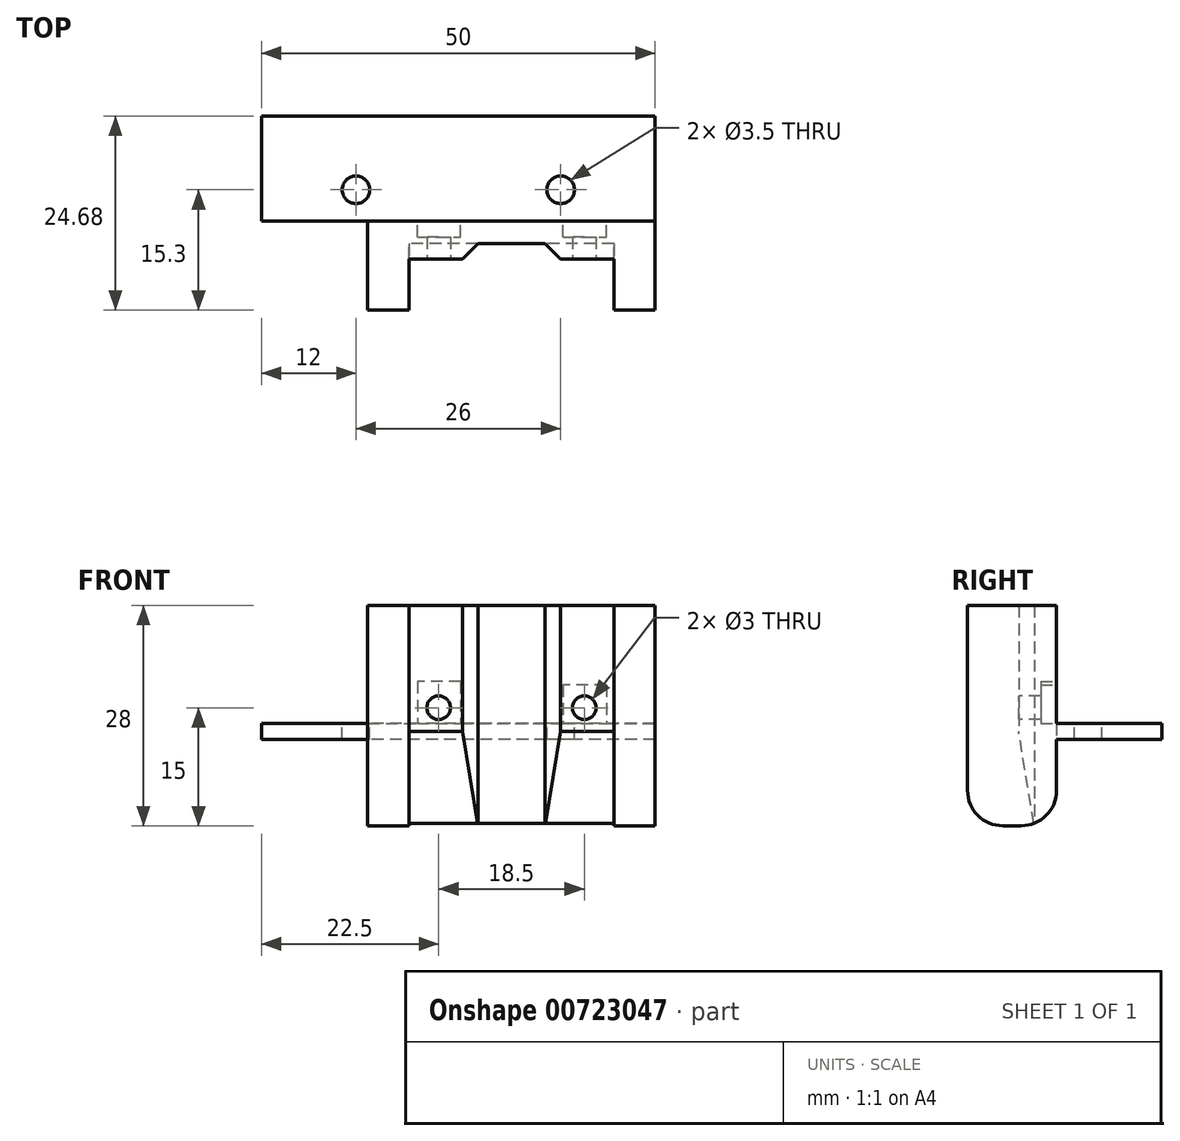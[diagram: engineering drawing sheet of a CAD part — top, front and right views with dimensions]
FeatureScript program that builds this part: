
annotation { "Feature Type Name" : "Feature", "Feature Type Description" : "" }
export const myFeature = defineFeature(function(context is Context, id is Id, definition is map)
    precondition{}
    {
        {
            var Q0;
            Q0=qCreatedBy(makeId("Right.planeOp"),FACE);
            var sketch = newSketch(context, id + "F0", { "sketchPlane" : qUnion([Q0])});
            skLineSegment(sketch, "E0", {"start": v(0, 0) * mm, "end": v(13.38, 0) * mm});
            skLineSegment(sketch, "E1", {"start": v(13.38, 0) * mm, "end": v(13.38, 2) * mm});
            skLineSegment(sketch, "E2", {"start": v(13.38, 2) * mm, "end": v(0, 2) * mm});
            skLineSegment(sketch, "E3", {"start": v(0, 2) * mm, "end": v(0, 0) * mm});
            skSolve(sketch);
        }
        {
            var Q0;
            Q0=makeQuery(id+"F0.imprint","IMPRINT",FACE,{"disambiguationData":[TD([[makeQuery(id+"F0.imprint","IMPRINT",EDGE,{"derivedFrom":sQuery(id+"F0.wireOp",EDGE,"E0")}),1.0]])]});
            extrude(context, id + "F1", {"entities" : qUnion([Q0]), "endBound" : BoundingType.SYMMETRIC, "depth" : 50 * mm});
        }
        {
            var Q0;
            Q0=makeQuery(id+"F1.opExtrude","SWEPT_FACE",FACE,{"disambiguationData":[OSD([sQuery(id+"F0.wireOp",EDGE,"E2")])]});
            var sketch = newSketch(context, id + "F2", { "sketchPlane" : qUnion([Q0])});
            skLineSegment(sketch, "E4", {"start": v(-25, 4) * mm, "end": v(25, 4) * mm, "construction": true});
            skLineSegment(sketch, "E5", {"start": v(0, 13.38) * mm, "end": v(0, 0) * mm, "construction": true});
            skCircle(sketch, "E6", {"center": v(-13, 4) * mm, "radius": 1.75 * mm});
            skCircle(sketch, "E7", {"center": v(13, 4) * mm, "radius": 1.75 * mm});
            skSolve(sketch);
        }
        {
            var Q0;
            Q0=qSketchRegion(id+"F2",true);
            extrude(context, id + "F3", {"entities" : qUnion([Q0]), "operationType" : NewBodyOperationType.REMOVE, "endBound" : BoundingType.UP_TO_NEXT, "oppositeDirection" : true, "depth" : 25 * mm});
        }
        {
            var Q0;
            Q0=qCreatedBy(makeId("Right.planeOp"),FACE);
            var sketch = newSketch(context, id + "F4", { "sketchPlane" : qUnion([Q0])});
            skLineSegment(sketch, "E8.bottom", {"start": v(0, 2) * mm, "end": v(-11.3, 2) * mm});
            skLineSegment(sketch, "E8.top", {"start": v(0, -11) * mm, "end": v(-11.3, -11) * mm});
            skLineSegment(sketch, "E8.left", {"start": v(0, 2) * mm, "end": v(0, -11) * mm});
            skLineSegment(sketch, "E8.right", {"start": v(-11.3, 2) * mm, "end": v(-11.3, -11) * mm});
            skSolve(sketch);
        }
        {
            var Q0;
            Q0=qSketchRegion(id+"F4",true);
            var Q1;
            Q1=makeQuery(id+"F1.opExtrude","CAP_FACE",FACE,{"disambiguationData":[OSD([sQuery(id+"F0.wireOp",EDGE,"E0"),sQuery(id+"F0.wireOp",EDGE,"E1"),sQuery(id+"F0.wireOp",EDGE,"E2"),sQuery(id+"F0.wireOp",EDGE,"E3")])],"isStart":false});
            extrude(context, id + "F5", {"entities" : qUnion([Q0]), "operationType" : NewBodyOperationType.ADD, "endBound" : BoundingType.UP_TO_SURFACE, "endBoundEntityFace" : qUnion([Q1]), "depth" : 36.5 * mm, "hasSecondDirection" : true, "secondDirectionOppositeDirection" : true, "secondDirectionDepth" : 11.5 * mm});
        }
        {
            var Q0;
            Q0=makeQuery(id+"F5.opExtrude","SWEPT_FACE",FACE,{"disambiguationData":[OSD([sQuery(id+"F4.wireOp",EDGE,"E8.top")])]});
            var sketch = newSketch(context, id + "F6", { "sketchPlane" : qUnion([Q0])});
            skLineSegment(sketch, "E9.bottom", {"start": v(-6.25, 11.3) * mm, "end": v(19.75, 11.3) * mm});
            skLineSegment(sketch, "E9.top", {"start": v(-6.25, 4.8) * mm, "end": v(19.75, 4.8) * mm});
            skLineSegment(sketch, "E9.left", {"start": v(-6.25, 11.3) * mm, "end": v(-6.25, 4.8) * mm});
            skLineSegment(sketch, "E9.right", {"start": v(19.75, 11.3) * mm, "end": v(19.75, 4.8) * mm});
            skLineSegment(sketch, "E10", {"start": v(6.75, 11.3) * mm, "end": v(6.75, 0) * mm, "construction": true});
            skSolve(sketch);
        }
        {
            var Q0;
            Q0=qSketchRegion(id+"F6",true);
            extrude(context, id + "F7", {"entities" : qUnion([Q0]), "operationType" : NewBodyOperationType.REMOVE, "endBound" : BoundingType.UP_TO_NEXT, "oppositeDirection" : true, "depth" : 25 * mm});
        }
        {
            var Q0;
            Q0=makeQuery(id+"F5.opExtrude","SWEPT_FACE",FACE,{"disambiguationData":[OSD([sQuery(id+"F4.wireOp",EDGE,"E8.top")])]});
            var sketch = newSketch(context, id + "F8", { "sketchPlane" : qUnion([Q0])});
            skLineSegment(sketch, "E11", {"start": v(6.75, 4.8) * mm, "end": v(6.75, 0) * mm, "construction": true});
            skLineSegment(sketch, "E12", {"start": v(0.5, 4.8) * mm, "end": v(2.5, 2.8) * mm});
            skLineSegment(sketch, "E13", {"start": v(2.5, 2.8) * mm, "end": v(11, 2.8) * mm});
            skLineSegment(sketch, "E14", {"start": v(11, 2.8) * mm, "end": v(13, 4.8) * mm});
            skLineSegment(sketch, "E15", {"start": v(13, 4.8) * mm, "end": v(0.5, 4.8) * mm});
            skSolve(sketch);
        }
        {
            var Q0;
            Q0=qSketchRegion(id+"F8",true);
            extrude(context, id + "F9", {"entities" : qUnion([Q0]), "operationType" : NewBodyOperationType.REMOVE, "endBound" : BoundingType.UP_TO_NEXT, "oppositeDirection" : true, "depth" : 25 * mm});
        }
        {
            var Q0;
            Q0=qCreatedBy(makeId("Right.planeOp"),FACE);
            var sketch = newSketch(context, id + "F10", { "sketchPlane" : qUnion([Q0])});
            skLineSegment(sketch, "E16", {"start": v(-2.8, -11) * mm, "end": v(-4.8, 1) * mm});
            skLineSegment(sketch, "E17", {"start": v(-4.8, 1) * mm, "end": v(-4.8, -11) * mm});
            skLineSegment(sketch, "E18", {"start": v(-4.8, -11) * mm, "end": v(-2.8, -11) * mm});
            skSolve(sketch);
        }
        {
            var Q0;
            Q0=qSketchRegion(id+"F10",true);
            var Q1;
            Q1=makeQuery(id+"F7.boolean.opBoolean","COPY",FACE,{"derivedFrom":makeQuery(id+"F7.opExtrude","SWEPT_FACE",FACE,{"disambiguationData":[OSD([sQuery(id+"F6.wireOp",EDGE,"E9.right")])]})});
            var Q2;
            Q2=makeQuery(id+"F7.boolean.opBoolean","COPY",FACE,{"derivedFrom":makeQuery(id+"F7.opExtrude","SWEPT_FACE",FACE,{"disambiguationData":[OSD([sQuery(id+"F6.wireOp",EDGE,"E9.left")])]})});
            extrude(context, id + "F11", {"entities" : qUnion([Q0]), "operationType" : NewBodyOperationType.REMOVE, "endBound" : BoundingType.UP_TO_SURFACE, "endBoundEntityFace" : qUnion([Q1]), "depth" : 25 * mm, "hasSecondDirection" : true, "secondDirectionBound" : SecondDirectionBoundingType.UP_TO_SURFACE, "secondDirectionOppositeDirection" : true, "secondDirectionBoundEntityFace" : qUnion([Q2]), "secondDirectionDepth" : 25 * mm});
        }
        {
            var Q0;
            Q0=makeQuery(id+"F9.boolean.opBoolean","SPLIT",FACE,{"disambiguationData":[TD([makeQuery(id+"F7.boolean.opBoolean","COPY",FACE,{"derivedFrom":makeQuery(id+"F7.opExtrude","SWEPT_FACE",FACE,{"disambiguationData":[OSD([sQuery(id+"F6.wireOp",EDGE,"E9.left")])]})})])],"derivedFrom":makeQuery(id+"F7.boolean.opBoolean","COPY",FACE,{"derivedFrom":makeQuery(id+"F7.opExtrude","SWEPT_FACE",FACE,{"disambiguationData":[OSD([sQuery(id+"F6.wireOp",EDGE,"E9.top")])]})})});
            var sketch = newSketch(context, id + "F12", { "sketchPlane" : qUnion([Q0])});
            skCircle(sketch, "E19", {"center": v(-2.5, 4) * mm, "radius": 1.38 * mm});
            skLineSegment(sketch, "E20", {"start": v(6.75, 2) * mm, "end": v(6.75, -11) * mm, "construction": true});
            skCircle(sketch, "E21.MirrorC", {"center": v(16, 4) * mm, "radius": 1.38 * mm});
            skLineSegment(sketch, "E22", {"start": v(6.75, -2) * mm, "end": v(24.95, -2) * mm});
            skLineSegment(sketch, "E23.bottom", {"start": v(18.75, 6.75) * mm, "end": v(13.25, 6.75) * mm});
            skLineSegment(sketch, "E23.top", {"start": v(18.75, 1.25) * mm, "end": v(13.25, 1.25) * mm});
            skLineSegment(sketch, "E23.left", {"start": v(18.75, 6.75) * mm, "end": v(18.75, 1.25) * mm});
            skLineSegment(sketch, "E23.right", {"start": v(13.25, 6.75) * mm, "end": v(13.25, 1.25) * mm});
            skLineSegment(sketch, "E24.bottom", {"start": v(-5.25, 6.75) * mm, "end": v(0.25, 6.75) * mm});
            skLineSegment(sketch, "E24.top", {"start": v(-5.25, 1.25) * mm, "end": v(0.25, 1.25) * mm});
            skLineSegment(sketch, "E24.left", {"start": v(-5.25, 6.75) * mm, "end": v(-5.25, 1.25) * mm});
            skLineSegment(sketch, "E24.right", {"start": v(0.25, 6.75) * mm, "end": v(0.25, 1.25) * mm});
            skSolve(sketch);
        }
        {
            var Q0;
            {var subQ0=sQuery(id+"F4.wireOp",EDGE,"E8.right");var subQ1=sQuery(id+"F4.wireOp",EDGE,"E8.top");Q0=makeQuery(id+"F7.boolean.opBoolean","SPLIT",EDGE,{"disambiguationData":[TD([makeQuery(id+"F7.opExtrude","SWEPT_FACE",FACE,{"disambiguationData":[OSD([sQuery(id+"F6.wireOp",EDGE,"E9.left")])]})])],"derivedFrom":makeQuery(id+"F5.opExtrude","SWEPT_EDGE",EDGE,{"disambiguationData":[OSD([subQ1,subQ0])]})});}
            var Q1;
            {var subQ0=sQuery(id+"F4.wireOp",EDGE,"E8.right");var subQ1=sQuery(id+"F4.wireOp",EDGE,"E8.top");Q1=makeQuery(id+"F7.boolean.opBoolean","SPLIT",EDGE,{"disambiguationData":[TD([makeQuery(id+"F7.opExtrude","SWEPT_FACE",FACE,{"disambiguationData":[OSD([sQuery(id+"F6.wireOp",EDGE,"E9.right")])]})])],"derivedFrom":makeQuery(id+"F5.opExtrude","SWEPT_EDGE",EDGE,{"disambiguationData":[OSD([subQ1,subQ0])]})});}
            var Q2;
            Q2=makeQuery(id+"F5.opExtrude","SWEPT_EDGE",EDGE,{"disambiguationData":[OSD([sQuery(id+"F4.wireOp",EDGE,"E8.top"),sQuery(id+"F4.wireOp",EDGE,"E8.left")])]});
            fillet(context, id + "F13", {"entities" : qUnion([Q0, Q1, Q2]), "radius" : 4.5 * mm, "tangentPropagation" : true, "allowEdgeOverflow" : false});
        }
        {
            var Q0;
            Q0=makeQuery(id+"F5.boolean.opBoolean","MERGE",FACE,{"derivedFrom":[makeQuery(id+"F1.opExtrude","SWEPT_FACE",FACE,{"disambiguationData":[OSD([sQuery(id+"F0.wireOp",EDGE,"E2")])]}),makeQuery(id+"F5.opExtrude","SWEPT_FACE",FACE,{"disambiguationData":[OSD([sQuery(id+"F4.wireOp",EDGE,"E8.bottom")])]})]});
            var sketch = newSketch(context, id + "F14", { "sketchPlane" : qUnion([Q0])});
            skLineSegment(sketch, "E25", {"start": v(-11.5, 0) * mm, "end": v(25, 0) * mm});
            skSolve(sketch);
        }
        {
            var Q0;
            {var subQ23=sQuery(id+"F14.wireOp",EDGE,"E25");Q0=makeQuery(id+"F14.imprint","IMPRINT",FACE,{"disambiguationData":[TD([[makeQuery(id+"F14.imprint","IMPRINT",EDGE,{"derivedFrom":subQ23}),-1.0]])]});}
            extrude(context, id + "F15", {"entities" : qUnion([Q0]), "operationType" : NewBodyOperationType.ADD, "depth" : 15 * mm, "offsetDistance" : 25 * mm});
        }
        {
            var Q0;
            Q0=makeQuery(id+"F15.opExtrude","SWEPT_FACE",FACE,{"disambiguationData":[OSD([sQuery(id+"F14.wireOp",EDGE,"E25")])]});
            var sketch = newSketch(context, id + "F16", { "sketchPlane" : qUnion([Q0])});
            skLineSegment(sketch, "E26.bottom", {"start": v(-18.8, 6.9) * mm, "end": v(-13.3, 6.9) * mm});
            skLineSegment(sketch, "E26.top", {"start": v(-18.8, 1.4) * mm, "end": v(-13.3, 1.4) * mm});
            skLineSegment(sketch, "E26.left", {"start": v(-18.8, 6.9) * mm, "end": v(-18.8, 1.4) * mm});
            skLineSegment(sketch, "E26.right", {"start": v(-13.3, 6.9) * mm, "end": v(-13.3, 1.4) * mm});
            skPoint(sketch, "E26.middle", {"position": v(-16.05, 4.15) * mm});
            skLineSegment(sketch, "E27.bottom", {"start": v(-0.3, 7.31) * mm, "end": v(5.2, 7.31) * mm});
            skLineSegment(sketch, "E27.top", {"start": v(-0.3, 1.81) * mm, "end": v(5.2, 1.81) * mm});
            skLineSegment(sketch, "E27.left", {"start": v(-0.3, 7.31) * mm, "end": v(-0.3, 1.81) * mm});
            skLineSegment(sketch, "E27.right", {"start": v(5.2, 7.31) * mm, "end": v(5.2, 1.81) * mm});
            skPoint(sketch, "E27.middle", {"position": v(2.45, 4.56) * mm});
            skSolve(sketch);
        }
        {
            var Q0;
            {var subQ0=sQuery(id+"F16.wireOp",EDGE,"E26.bottom");Q0=makeQuery(id+"F16.imprint","IMPRINT",FACE,{"disambiguationData":[TD([[makeQuery(id+"F16.imprint","IMPRINT",EDGE,{"derivedFrom":subQ0}),-1.0]])]});}
            var Q1;
            {var subQ0=sQuery(id+"F16.wireOp",EDGE,"E27.bottom");Q1=makeQuery(id+"F16.imprint","IMPRINT",FACE,{"disambiguationData":[TD([[makeQuery(id+"F16.imprint","IMPRINT",EDGE,{"derivedFrom":subQ0}),-1.0]])]});}
            extrude(context, id + "F17", {"entities" : qUnion([Q0, Q1]), "operationType" : NewBodyOperationType.ADD, "oppositeDirection" : true, "depth" : 2 * mm, "offsetDistance" : 25 * mm});
        }
        {
            var Q0;
            {var subQ0=sQuery(id+"F16.wireOp",EDGE,"E26.bottom");Q0=makeQuery(id+"F16.imprint","IMPRINT",FACE,{"disambiguationData":[TD([[makeQuery(id+"F16.imprint","IMPRINT",EDGE,{"derivedFrom":subQ0}),-1.0]])]});}
            var Q1;
            {var subQ0=sQuery(id+"F16.wireOp",EDGE,"E27.bottom");Q1=makeQuery(id+"F16.imprint","IMPRINT",FACE,{"disambiguationData":[TD([[makeQuery(id+"F16.imprint","IMPRINT",EDGE,{"derivedFrom":subQ0}),-1.0]])]});}
            extrude(context, id + "F18", {"entities" : qUnion([Q0, Q1]), "operationType" : NewBodyOperationType.REMOVE, "oppositeDirection" : true, "depth" : 2 * mm, "offsetDistance" : 25 * mm});
        }
        {
            var Q0;
            Q0=sQuery(id+"F12.wireOp",VERTEX,"E21.MirrorC.center");
            var Q1;
            Q1=sQuery(id+"F12.wireOp",VERTEX,"E19.center");
            var Q2;
            Q2=makeQuery(id+"F1.opExtrude","SWEPT_BODY",BODY,{"disambiguationData":[OSD([sQuery(id+"F0.wireOp",EDGE,"E0"),sQuery(id+"F0.wireOp",EDGE,"E1"),sQuery(id+"F0.wireOp",EDGE,"E2"),sQuery(id+"F0.wireOp",EDGE,"E3")])]});
            hole(context, id + "F19", {"style" : HoleStyle.SIMPLE, "endStyle" : HoleEndStyle.THROUGH, "holeDiameter" : 3 * mm, "majorDiameter" : 5 * mm, "isTappedThrough" : true, "tappedDepth" : 12 * mm, "tapClearance" : 3, "locations" : qUnion([Q0, Q1]), "scope" : qUnion([Q2])});
        }
    });
